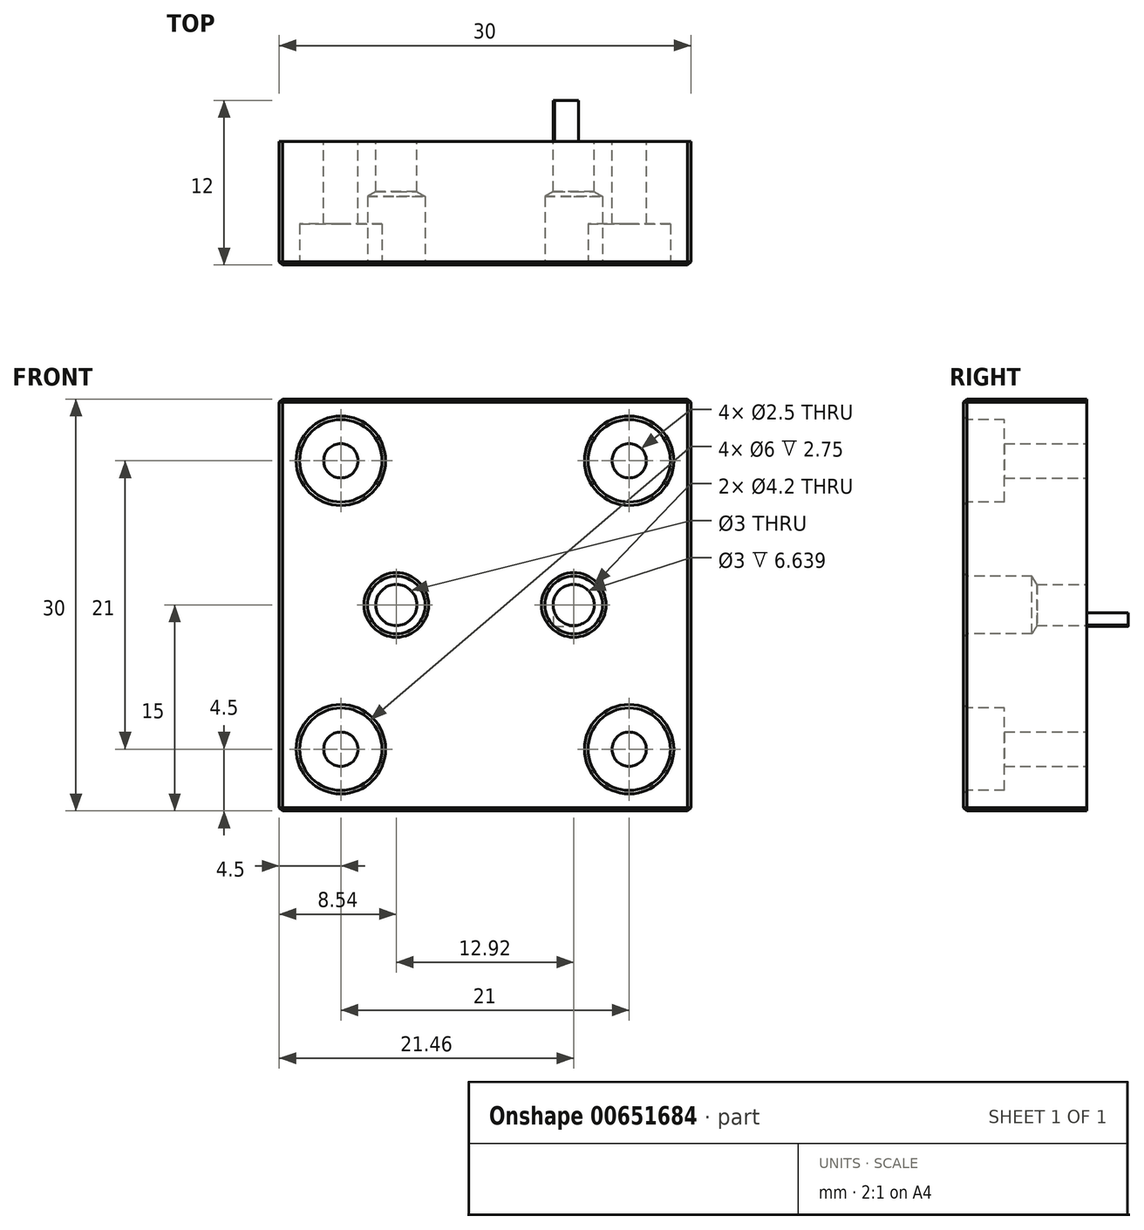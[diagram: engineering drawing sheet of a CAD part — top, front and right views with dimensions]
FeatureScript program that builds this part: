
annotation { "Feature Type Name" : "Feature", "Feature Type Description" : "" }
export const myFeature = defineFeature(function(context is Context, id is Id, definition is map)
    precondition{}
    {
        {
            var Q0;
            Q0=qCreatedBy(makeId("Front.planeOp"),FACE);
            var sketch = newSketch(context, id + "F0", { "sketchPlane" : qUnion([Q0])});
            skLineSegment(sketch, "E0.bottom", {"start": v(0, 0) * mm, "end": v(30, 0) * mm});
            skLineSegment(sketch, "E0.top", {"start": v(0, -30) * mm, "end": v(30, -30) * mm});
            skLineSegment(sketch, "E0.left", {"start": v(0, 0) * mm, "end": v(0, -30) * mm});
            skLineSegment(sketch, "E0.right", {"start": v(30, 0) * mm, "end": v(30, -30) * mm});
            skLineSegment(sketch, "E1", {"start": v(15, 0) * mm, "end": v(15, -30) * mm, "construction": true});
            skCircle(sketch, "E2", {"center": v(15, -16.07) * mm, "radius": 3 * mm});
            skCircle(sketch, "E3", {"center": v(15, -15) * mm, "radius": 10 * mm});
            skSolve(sketch);
        }
        {
            var Q0;
            Q0=makeQuery(id+"F0.imprint","IMPRINT",FACE,{"disambiguationData":[TD([[makeQuery(id+"F0.imprint","IMPRINT",EDGE,{"derivedFrom":sQuery(id+"F0.wireOp",EDGE,"E0.bottom")}),-1.0]])]});
            var Q1;
            Q1=makeQuery(id+"F0.imprint","IMPRINT",FACE,{"disambiguationData":[TD([[makeQuery(id+"F0.imprint","IMPRINT",EDGE,{"derivedFrom":sQuery(id+"F0.wireOp",EDGE,"E2")}),-1.0]])]});
            var Q2;
            Q2=makeQuery(id+"F0.imprint","IMPRINT",FACE,{"disambiguationData":[TD([[makeQuery(id+"F0.imprint","IMPRINT",EDGE,{"derivedFrom":sQuery(id+"F0.wireOp",EDGE,"E2")}),1.0]])]});
            extrude(context, id + "F1", {"entities" : qUnion([Q0, Q1, Q2]), "depth" : 12 * mm, "offsetDistance" : 25 * mm});
        }
        {
            var Q0;
            Q0=makeQuery(id+"F1.opExtrude","CAP_FACE",FACE,{"disambiguationData":[OSD([sQuery(id+"F0.wireOp",EDGE,"E0.bottom"),sQuery(id+"F0.wireOp",EDGE,"E0.top"),sQuery(id+"F0.wireOp",EDGE,"E0.left"),sQuery(id+"F0.wireOp",EDGE,"E0.right"),sQuery(id+"F0.wireOp",EDGE,"E2")])],"isStart":true});
            var sketch = newSketch(context, id + "F2", { "sketchPlane" : qUnion([Q0])});
            skLineSegment(sketch, "E4", {"start": v(-4.5, 0) * mm, "end": v(-4.5, -4.5) * mm, "construction": true});
            skLineSegment(sketch, "E5", {"start": v(-4.5, -4.5) * mm, "end": v(0, -4.5) * mm, "construction": true});
            skCircle(sketch, "E6", {"center": v(-4.5, -4.5) * mm, "radius": 1.25 * mm});
            skLineSegment(sketch, "E7", {"start": v(-25.5, 0) * mm, "end": v(-25.5, -4.5) * mm, "construction": true});
            skLineSegment(sketch, "E8", {"start": v(-25.5, -4.5) * mm, "end": v(-30, -4.5) * mm, "construction": true});
            skLineSegment(sketch, "E9", {"start": v(-30, -25.5) * mm, "end": v(-25.5, -25.5) * mm, "construction": true});
            skLineSegment(sketch, "E10", {"start": v(-4.5, -30) * mm, "end": v(-4.5, -25.5) * mm, "construction": true});
            skLineSegment(sketch, "E11", {"start": v(-4.5, -25.5) * mm, "end": v(0, -25.5) * mm, "construction": true});
            skLineSegment(sketch, "E12", {"start": v(-25.5, -25.5) * mm, "end": v(-25.5, -30) * mm, "construction": true});
            skCircle(sketch, "E13", {"center": v(-25.5, -4.5) * mm, "radius": 1.25 * mm});
            skCircle(sketch, "E14", {"center": v(-25.5, -25.5) * mm, "radius": 1.25 * mm});
            skCircle(sketch, "E15", {"center": v(-4.5, -25.5) * mm, "radius": 1.25 * mm});
            skSolve(sketch);
        }
        {
            var Q0;
            Q0=makeQuery(id+"F2.imprint","IMPRINT",FACE,{"disambiguationData":[TD([[makeQuery(id+"F2.imprint","IMPRINT",EDGE,{"derivedFrom":sQuery(id+"F2.wireOp",EDGE,"E6")}),1.0]])]});
            var Q1;
            Q1=makeQuery(id+"F2.imprint","IMPRINT",FACE,{"disambiguationData":[TD([[makeQuery(id+"F2.imprint","IMPRINT",EDGE,{"derivedFrom":sQuery(id+"F2.wireOp",EDGE,"E13")}),1.0]])]});
            var Q2;
            Q2=makeQuery(id+"F2.imprint","IMPRINT",FACE,{"disambiguationData":[TD([[makeQuery(id+"F2.imprint","IMPRINT",EDGE,{"derivedFrom":sQuery(id+"F2.wireOp",EDGE,"E14")}),1.0]])]});
            var Q3;
            Q3=makeQuery(id+"F2.imprint","IMPRINT",FACE,{"disambiguationData":[TD([[makeQuery(id+"F2.imprint","IMPRINT",EDGE,{"derivedFrom":sQuery(id+"F2.wireOp",EDGE,"E15")}),1.0]])]});
            extrude(context, id + "F3", {"entities" : qUnion([Q0, Q1, Q2, Q3]), "operationType" : NewBodyOperationType.REMOVE, "oppositeDirection" : true, "depth" : 20 * mm, "offsetDistance" : 25 * mm});
        }
        {
            var Q0;
            Q0=makeQuery(id+"F0.imprint","IMPRINT",FACE,{"disambiguationData":[TD([[makeQuery(id+"F0.imprint","IMPRINT",EDGE,{"derivedFrom":sQuery(id+"F0.wireOp",EDGE,"E2")}),1.0]])]});
            extrude(context, id + "F4", {"entities" : qUnion([Q0]), "operationType" : NewBodyOperationType.REMOVE, "depth" : 3 * mm, "offsetDistance" : 25 * mm});
        }
        {
            var Q0;
            Q0=makeQuery(id+"F1.opExtrude","CAP_FACE",FACE,{"disambiguationData":[OSD([sQuery(id+"F0.wireOp",EDGE,"E0.bottom"),sQuery(id+"F0.wireOp",EDGE,"E0.top"),sQuery(id+"F0.wireOp",EDGE,"E0.left"),sQuery(id+"F0.wireOp",EDGE,"E0.right")])],"isStart":false});
            var sketch = newSketch(context, id + "F5", { "sketchPlane" : qUnion([Q0])});
            skCircle(sketch, "E16", {"center": v(4.5, -4.5) * mm, "radius": 3 * mm});
            skCircle(sketch, "E17", {"center": v(25.5, -4.5) * mm, "radius": 3 * mm});
            skCircle(sketch, "E18", {"center": v(25.5, -25.5) * mm, "radius": 3 * mm});
            skCircle(sketch, "E19", {"center": v(4.5, -25.5) * mm, "radius": 3 * mm});
            skSolve(sketch);
        }
        {
            var Q0;
            Q0=makeQuery(id+"F5.imprint","IMPRINT",FACE,{"disambiguationData":[TD([[makeQuery(id+"F5.imprint","IMPRINT",EDGE,{"derivedFrom":sQuery(id+"F5.wireOp",EDGE,"E16")}),1.0]])]});
            var Q1;
            Q1=makeQuery(id+"F5.imprint","IMPRINT",FACE,{"disambiguationData":[TD([[makeQuery(id+"F5.imprint","IMPRINT",EDGE,{"derivedFrom":sQuery(id+"F5.wireOp",EDGE,"E17")}),1.0]])]});
            var Q2;
            Q2=makeQuery(id+"F5.imprint","IMPRINT",FACE,{"disambiguationData":[TD([[makeQuery(id+"F5.imprint","IMPRINT",EDGE,{"derivedFrom":sQuery(id+"F5.wireOp",EDGE,"E19")}),1.0]])]});
            var Q3;
            Q3=makeQuery(id+"F5.imprint","IMPRINT",FACE,{"disambiguationData":[TD([[makeQuery(id+"F5.imprint","IMPRINT",EDGE,{"derivedFrom":sQuery(id+"F5.wireOp",EDGE,"E18")}),1.0]])]});
            extrude(context, id + "F6", {"entities" : qUnion([Q0, Q1, Q2, Q3]), "operationType" : NewBodyOperationType.REMOVE, "oppositeDirection" : true, "depth" : 3 * mm, "offsetDistance" : 25 * mm});
        }
        {
            var Q0;
            Q0=makeQuery(id+"F1.opExtrude","CAP_FACE",FACE,{"disambiguationData":[OSD([sQuery(id+"F0.wireOp",EDGE,"E0.bottom"),sQuery(id+"F0.wireOp",EDGE,"E0.top"),sQuery(id+"F0.wireOp",EDGE,"E0.left"),sQuery(id+"F0.wireOp",EDGE,"E0.right")])],"isStart":true});
            var sketch = newSketch(context, id + "F7", { "sketchPlane" : qUnion([Q0])});
            skLineSegment(sketch, "E20", {"start": v(0, -15) * mm, "end": v(-30, -15) * mm, "construction": true});
            skLineSegment(sketch, "E21", {"start": v(-15, 0) * mm, "end": v(-15, -30) * mm, "construction": true});
            skPoint(sketch, "E22", {"position": v(-15, -15) * mm});
            skArc(sketch, "E23", {"start": v(-21.13, -9.86) * mm, "mid": v(-22.82, -16.69) * mm, "end": v(-18.46, -22.21) * mm});
            skArc(sketch, "E24", {"start": v(-18.25, -12.27) * mm, "mid": v(-19.98, -16.53) * mm, "end": v(-17.5, -20.4) * mm});
            skArc(sketch, "E25", {"start": v(-18.42, -12.42) * mm, "mid": v(-18.42, -9.7) * mm, "end": v(-21.13, -9.86) * mm});
            skLineSegment(sketch, "E26", {"start": v(-19.7, -11.06) * mm, "end": v(-15, -15) * mm, "construction": true});
            skArc(sketch, "E27", {"start": v(-8.87, -9.86) * mm, "mid": v(-11.58, -9.7) * mm, "end": v(-11.58, -12.42) * mm});
            skLineSegment(sketch, "E28", {"start": v(-15, -15) * mm, "end": v(-10.3, -11.06) * mm, "construction": true});
            skLineSegment(sketch, "E29", {"start": v(-19.7, -11.06) * mm, "end": v(-10.3, -11.06) * mm, "construction": true});
            skArc(sketch, "E30", {"start": v(-18.46, -22.21) * mm, "mid": v(-17.1, -21.77) * mm, "end": v(-17.5, -20.4) * mm});
            skArc(sketch, "E31", {"start": v(-12.5, -20.4) * mm, "mid": v(-12.9, -21.77) * mm, "end": v(-11.54, -22.21) * mm});
            skLineSegment(sketch, "E32", {"start": v(-15, -16.07) * mm, "end": v(-18.01, -21.29) * mm, "construction": true});
            skLineSegment(sketch, "E33", {"start": v(-18.01, -21.29) * mm, "end": v(-11.99, -21.29) * mm, "construction": true});
            skLineSegment(sketch, "E34", {"start": v(-15, -16.07) * mm, "end": v(-11.99, -21.29) * mm, "construction": true});
            skArc(sketch, "E35.trimOffspring", {"start": v(-12.5, -20.4) * mm, "mid": v(-10.02, -16.53) * mm, "end": v(-11.75, -12.27) * mm});
            skArc(sketch, "E36.trimOffspring", {"start": v(-11.54, -22.21) * mm, "mid": v(-7.18, -16.69) * mm, "end": v(-8.87, -9.86) * mm});
            skCircle(sketch, "E37", {"center": v(-21.46, -15) * mm, "radius": 1.54 * mm, "construction": true});
            skCircle(sketch, "E38", {"center": v(-8.54, -15) * mm, "radius": 1.54 * mm, "construction": true});
            skLineSegment(sketch, "E39", {"start": v(-15, -16.07) * mm, "end": v(-21.5, -16.07) * mm, "construction": true});
            skArc(sketch, "E40.0.startCap", {"start": v(-15, -15.57) * mm, "mid": v(-14.5, -16.07) * mm, "end": v(-15, -16.57) * mm});
            skArc(sketch, "E40.0.endCap", {"start": v(-21.5, -16.57) * mm, "mid": v(-22, -16.07) * mm, "end": v(-21.5, -15.57) * mm});
            skLineSegment(sketch, "E40.0.left", {"start": v(-15, -16.57) * mm, "end": v(-21.5, -16.57) * mm});
            skLineSegment(sketch, "E40.0.right", {"start": v(-15, -15.57) * mm, "end": v(-21.5, -15.57) * mm});
            skSolve(sketch);
        }
        {
            var Q0;
            {var subQ0=sQuery(id+"F7.wireOp",EDGE,"E40.0.right");var subQ1=sQuery(id+"F7.wireOp",EDGE,"E24");var subQ2=makeQuery(id+"F7.imprint","INTERSECT",VERTEX,{"derivedFrom":[subQ1,subQ0]});Q0=makeQuery(id+"F7.imprint","IMPRINT",FACE,{"disambiguationData":[TD([[makeQuery(id+"F7.imprint","IMPRINT",EDGE,{"disambiguationData":[TD([[subQ2,-1.0]])],"derivedFrom":subQ1}),1.0]])]});}
            extrude(context, id + "F8", {"entities" : qUnion([Q0]), "operationType" : NewBodyOperationType.REMOVE, "oppositeDirection" : true, "depth" : 3 * mm, "offsetDistance" : 25 * mm});
        }
        {
            var Q0;
            {var subQ0=sQuery(id+"F7.wireOp",EDGE,"8ySW9AUi-8OTO-dBn3-pUTx-747DyvfBu4kE");Q0=makeQuery(id+"F7.imprint","IMPRINT",FACE,{"disambiguationData":[TD([[makeQuery(id+"F7.imprint","IMPRINT",EDGE,{"derivedFrom":subQ0}),-1.0]])]});}
            var Q1;
            Q1=makeQuery(id+"F7.imprint","IMPRINT",FACE,{"disambiguationData":[TD([[makeQuery(id+"F7.imprint","IMPRINT",EDGE,{"derivedFrom":sQuery(id+"F7.wireOp",EDGE,"E23")}),1.0]])]});
            var Q2;
            {var subQ0=sQuery(id+"F7.wireOp",EDGE,"E27");Q2=makeQuery(id+"F7.imprint","IMPRINT",FACE,{"disambiguationData":[TD([[makeQuery(id+"F7.imprint","IMPRINT",EDGE,{"derivedFrom":subQ0}),1.0]])]});}
            var Q3;
            {var subQ5=sQuery(id+"F7.wireOp",EDGE,"E40.0.endCap");Q3=makeQuery(id+"F7.imprint","IMPRINT",FACE,{"disambiguationData":[TD([[makeQuery(id+"F7.imprint","IMPRINT",EDGE,{"derivedFrom":subQ5}),-1.0]])]});}
            extrude(context, id + "F9", {"entities" : qUnion([Q0, Q1, Q2, Q3]), "operationType" : NewBodyOperationType.REMOVE, "oppositeDirection" : true, "depth" : 3 * mm, "offsetDistance" : 25 * mm});
        }
        {
            var Q0;
            Q0=makeQuery(id+"F1.opExtrude","SWEPT_FACE",FACE,{"disambiguationData":[OSD([sQuery(id+"F0.wireOp",EDGE,"E0.right")])]});
            var sketch = newSketch(context, id + "F10", { "sketchPlane" : qUnion([Q0])});
            skLineSegment(sketch, "E41", {"start": v(-12, -12) * mm, "end": v(0, -12) * mm, "construction": true});
            skPoint(sketch, "E42", {"position": v(-6, -12) * mm});
            skSolve(sketch);
        }
        {
            var Q0;
            Q0=makeQuery(id+"F1.opExtrude","SWEPT_FACE",FACE,{"disambiguationData":[OSD([sQuery(id+"F0.wireOp",EDGE,"E0.left")])]});
            var sketch = newSketch(context, id + "F11", { "sketchPlane" : qUnion([Q0])});
            skLineSegment(sketch, "E43", {"start": v(0, -12) * mm, "end": v(12, -12) * mm, "construction": true});
            skPoint(sketch, "E44", {"position": v(6, -12) * mm});
            skSolve(sketch);
        }
        {
            var Q0;
            Q0=sQuery(id+"F7.wireOp",VERTEX,"E37.center");
            var Q1;
            Q1=sQuery(id+"F7.wireOp",VERTEX,"E38.center");
            var Q2;
            Q2=makeQuery(id+"F1.opExtrude","SWEPT_BODY",BODY,{"disambiguationData":[OSD([sQuery(id+"F0.wireOp",EDGE,"E0.bottom"),sQuery(id+"F0.wireOp",EDGE,"E0.top"),sQuery(id+"F0.wireOp",EDGE,"E0.left"),sQuery(id+"F0.wireOp",EDGE,"E0.right")])]});
            hole(context, id + "F12", {"style" : HoleStyle.SIMPLE, "endStyle" : HoleEndStyle.THROUGH, "holeDiameter" : 3 * mm, "majorDiameter" : 5 * mm, "isTappedThrough" : true, "tappedDepth" : 12 * mm, "tapClearance" : 3, "locations" : qUnion([Q0, Q1]), "scope" : qUnion([Q2])});
        }
        {
            var Q0;
            Q0=makeQuery(id+"F1.opExtrude","CAP_FACE",FACE,{"disambiguationData":[OSD([sQuery(id+"F0.wireOp",EDGE,"E0.bottom"),sQuery(id+"F0.wireOp",EDGE,"E0.top"),sQuery(id+"F0.wireOp",EDGE,"E0.left"),sQuery(id+"F0.wireOp",EDGE,"E0.right")])],"isStart":false});
            var sketch = newSketch(context, id + "F13", { "sketchPlane" : qUnion([Q0])});
            skPoint(sketch, "E45", {"position": v(8.54, -15) * mm});
            skPoint(sketch, "E46", {"position": v(21.46, -15) * mm});
            skSolve(sketch);
        }
        {
            var Q0;
            Q0=sQuery(id+"F13.wireOp",VERTEX,"E45");
            var Q1;
            Q1=sQuery(id+"F13.wireOp",VERTEX,"E46");
            var Q2;
            Q2=makeQuery(id+"F1.opExtrude","SWEPT_BODY",BODY,{"disambiguationData":[OSD([sQuery(id+"F0.wireOp",EDGE,"E0.bottom"),sQuery(id+"F0.wireOp",EDGE,"E0.top"),sQuery(id+"F0.wireOp",EDGE,"E0.left"),sQuery(id+"F0.wireOp",EDGE,"E0.right")])]});
            hole(context, id + "F14", {"style" : HoleStyle.SIMPLE, "endStyle" : HoleEndStyle.BLIND, "holeDiameter" : 4.2 * mm, "majorDiameter" : 5 * mm, "holeDepth" : 5 * mm, "isTappedThrough" : true, "tappedDepth" : 12 * mm, "tapClearance" : 3, "locations" : qUnion([Q0, Q1]), "scope" : qUnion([Q2])});
        }
        {
            var Q0;
            Q0=makeQuery(id+"F1.opExtrude","CAP_FACE",FACE,{"disambiguationData":[OSD([sQuery(id+"F0.wireOp",EDGE,"E0.bottom"),sQuery(id+"F0.wireOp",EDGE,"E0.top"),sQuery(id+"F0.wireOp",EDGE,"E0.left"),sQuery(id+"F0.wireOp",EDGE,"E0.right")])],"isStart":false});
            var Q1;
            Q1=makeQuery(id+"F1.opExtrude","SWEPT_EDGE",EDGE,{"disambiguationData":[OSD([sQuery(id+"F0.wireOp",EDGE,"E0.bottom"),sQuery(id+"F0.wireOp",EDGE,"E0.left")])]});
            var Q2;
            Q2=makeQuery(id+"F1.opExtrude","SWEPT_EDGE",EDGE,{"disambiguationData":[OSD([sQuery(id+"F0.wireOp",EDGE,"E0.bottom"),sQuery(id+"F0.wireOp",EDGE,"E0.right")])]});
            var Q3;
            Q3=makeQuery(id+"F1.opExtrude","SWEPT_EDGE",EDGE,{"disambiguationData":[OSD([sQuery(id+"F0.wireOp",EDGE,"E0.top"),sQuery(id+"F0.wireOp",EDGE,"E0.right")])]});
            var Q4;
            Q4=makeQuery(id+"F1.opExtrude","SWEPT_EDGE",EDGE,{"disambiguationData":[OSD([sQuery(id+"F0.wireOp",EDGE,"E0.top"),sQuery(id+"F0.wireOp",EDGE,"E0.left")])]});
            var Q5;
            Q5=makeQuery(id+"FpA3KyLedf2lyLR_1.hole-1.boolean.opBoolean","COPY",EDGE,{"derivedFrom":makeQuery(id+"FpA3KyLedf2lyLR_1.hole-1.opRevolve","SWEPT_EDGE",EDGE,{"disambiguationData":[OSD([sQuery(id+"FpA3KyLedf2lyLR_1.hole-1.sketch.wireOp",EDGE,"core_line_2"),sQuery(id+"FpA3KyLedf2lyLR_1.hole-1.sketch.wireOp",EDGE,"core_line_3")])]})});
            var Q6;
            Q6=makeQuery(id+"FpA3KyLedf2lyLR_1.hole-0.boolean.opBoolean","COPY",EDGE,{"derivedFrom":makeQuery(id+"FpA3KyLedf2lyLR_1.hole-0.opRevolve","SWEPT_EDGE",EDGE,{"disambiguationData":[OSD([sQuery(id+"FpA3KyLedf2lyLR_1.hole-0.sketch.wireOp",EDGE,"core_line_2"),sQuery(id+"FpA3KyLedf2lyLR_1.hole-0.sketch.wireOp",EDGE,"core_line_3")])]})});
            var Q7;
            Q7=makeQuery(id+"F12.hole-1.boolean.opBoolean","INTERSECT",EDGE,{"derivedFrom":[makeQuery(id+"F1.opExtrude","CAP_FACE",FACE,{"disambiguationData":[OSD([sQuery(id+"F0.wireOp",EDGE,"E0.bottom"),sQuery(id+"F0.wireOp",EDGE,"E0.top"),sQuery(id+"F0.wireOp",EDGE,"E0.left"),sQuery(id+"F0.wireOp",EDGE,"E0.right")])],"isStart":false}),makeQuery(id+"F12.hole-1.opRevolve","SWEPT_FACE",FACE,{"disambiguationData":[OSD([sQuery(id+"F12.hole-1.sketch.wireOp",EDGE,"core_line_2")])]})]});
            var Q8;
            Q8=makeQuery(id+"F12.hole-0.boolean.opBoolean","INTERSECT",EDGE,{"derivedFrom":[makeQuery(id+"F1.opExtrude","CAP_FACE",FACE,{"disambiguationData":[OSD([sQuery(id+"F0.wireOp",EDGE,"E0.bottom"),sQuery(id+"F0.wireOp",EDGE,"E0.top"),sQuery(id+"F0.wireOp",EDGE,"E0.left"),sQuery(id+"F0.wireOp",EDGE,"E0.right")])],"isStart":false}),makeQuery(id+"F12.hole-0.opRevolve","SWEPT_FACE",FACE,{"disambiguationData":[OSD([sQuery(id+"F12.hole-0.sketch.wireOp",EDGE,"core_line_2")])]})]});
            chamfer(context, id + "F15", {"entities" : qUnion([Q0, Q1, Q2, Q3, Q4, Q5, Q6, Q7, Q8]), "width" : .25 * mm, "tangentPropagation" : true});
        }
    });
